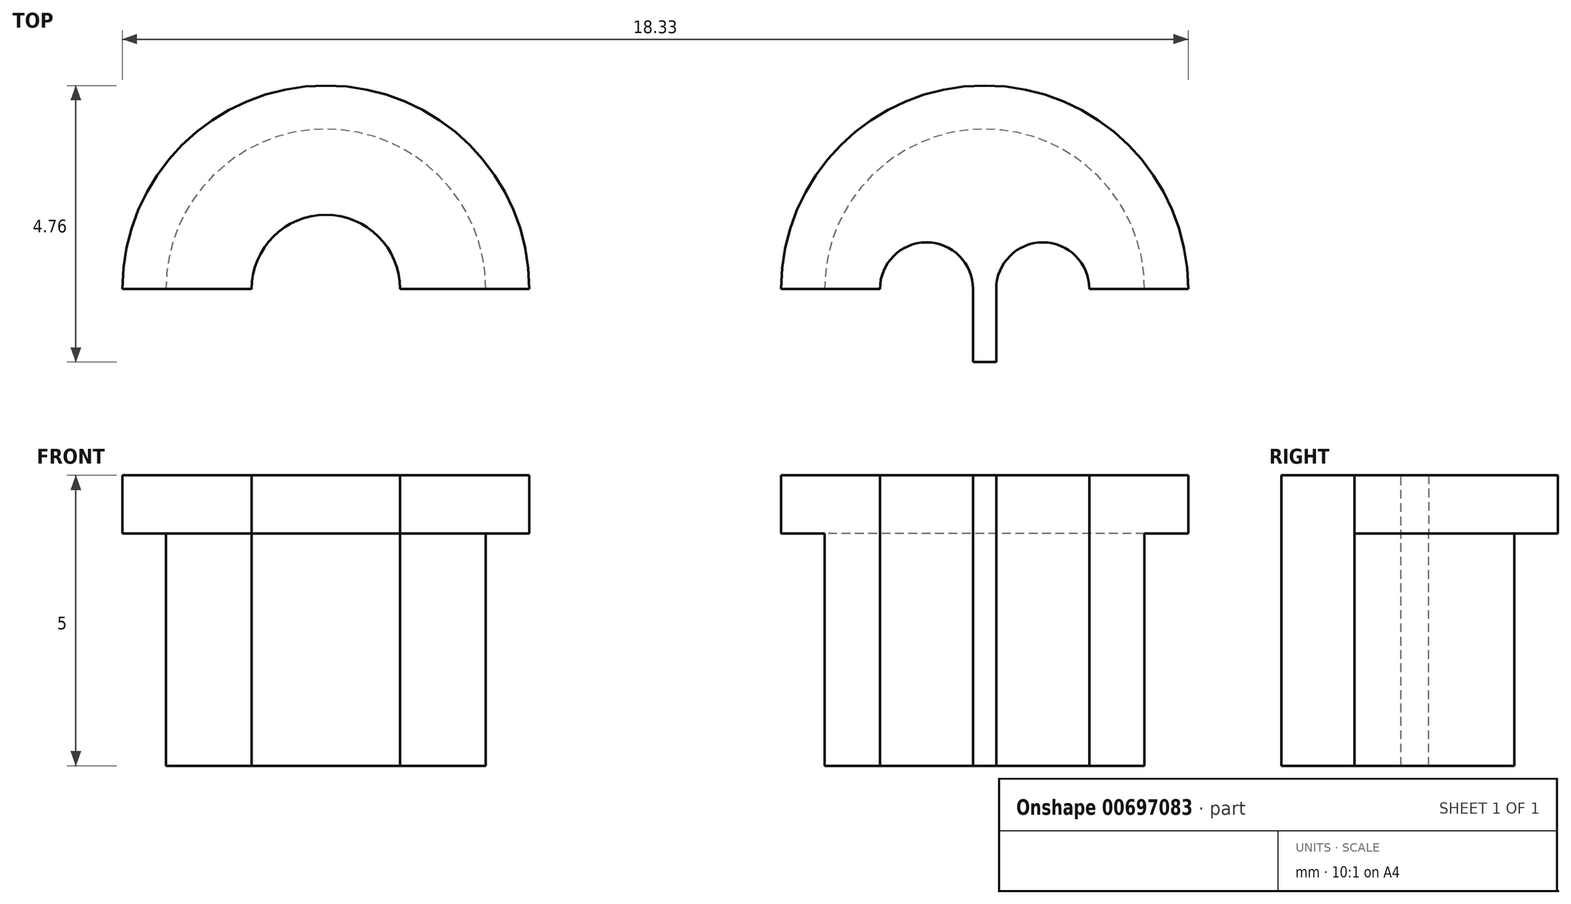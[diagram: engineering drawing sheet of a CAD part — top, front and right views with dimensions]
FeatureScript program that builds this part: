
annotation { "Feature Type Name" : "Feature", "Feature Type Description" : "" }
export const myFeature = defineFeature(function(context is Context, id is Id, definition is map)
    precondition{}
    {
        {
            assignVariable(context, id + "F0", {"name" : "thickness_washer", "anyValue" : 4 * mm});
        }
        {
            assignVariable(context, id + "F1", {"name" : "lip_thickness", "anyValue" : 1 * mm});
        }
        {
            var Q0;
            Q0=qCreatedBy(makeId("Top.planeOp"),FACE);
            var sketch = newSketch(context, id + "F2", { "sketchPlane" : qUnion([Q0])});
            skArc(sketch, "E0", {"start": v(2.75, 0) * mm, "mid": v(0, 2.75) * mm, "end": v(-2.75, 0) * mm});
            skPoint(sketch, "E1", {"position": v(-1, 0) * mm});
            skPoint(sketch, "E2", {"position": v(1, 0) * mm});
            skLineSegment(sketch, "E3", {"start": v(-2.75, 0) * mm, "end": v(-1.8, 0) * mm});
            skArc(sketch, "E4", {"start": v(-0.2, 0) * mm, "mid": v(-1, 0.8) * mm, "end": v(-1.8, 0) * mm});
            skArc(sketch, "E5", {"start": v(1.8, 0) * mm, "mid": v(1, 0.8) * mm, "end": v(0.2, 0) * mm});
            skLineSegment(sketch, "E6.trimOffspring", {"start": v(1.8, 0) * mm, "end": v(2.75, 0) * mm});
            skArc(sketch, "E7", {"start": v(3.5, 0) * mm, "mid": v(0, 3.5) * mm, "end": v(-3.5, 0) * mm});
            skLineSegment(sketch, "E8", {"start": v(3.5, 0) * mm, "end": v(0.2, 0) * mm});
            skLineSegment(sketch, "E9.trimOffspring", {"start": v(-0.2, 0) * mm, "end": v(-3.5, 0) * mm});
            skLineSegment(sketch, "E10", {"start": v(-0.2, 0) * mm, "end": v(-0.2, -1.26) * mm});
            skLineSegment(sketch, "E11", {"start": v(-0.2, -1.26) * mm, "end": v(0.2, -1.26) * mm});
            skLineSegment(sketch, "E12", {"start": v(0.2, -1.26) * mm, "end": v(0.2, 0) * mm});
            skArc(sketch, "E13", {"start": v(-8.58, 0) * mm, "mid": v(-11.33, 2.75) * mm, "end": v(-14.08, 0) * mm});
            skArc(sketch, "E14", {"start": v(-7.83, 0) * mm, "mid": v(-11.33, 3.5) * mm, "end": v(-14.83, 0) * mm});
            skLineSegment(sketch, "E15", {"start": v(-14.83, 0) * mm, "end": v(-14.08, 0) * mm});
            skLineSegment(sketch, "E16", {"start": v(-8.58, 0) * mm, "end": v(-7.83, 0) * mm});
            skArc(sketch, "E17", {"start": v(-10.05, 0) * mm, "mid": v(-11.33, 1.28) * mm, "end": v(-12.6, 0) * mm});
            skLineSegment(sketch, "E18", {"start": v(-14.08, 0) * mm, "end": v(-12.6, 0) * mm});
            skLineSegment(sketch, "E19", {"start": v(-10.05, 0) * mm, "end": v(-8.58, 0) * mm});
            skSolve(sketch);
        }
        {
            var Q0;
            Q0=makeQuery(id+"F2.imprint","IMPRINT",FACE,{"disambiguationData":[TD([[makeQuery(id+"F2.imprint","IMPRINT",EDGE,{"derivedFrom":sQuery(id+"F2.wireOp",EDGE,"E0")}),1.0]])]});
            extrude(context, id + "F3", {"entities" : qUnion([Q0]), "oppositeDirection" : true, "depth" : getVariable(context, 'thickness_washer'), "offsetDistance" : 25 * mm});
        }
        {
            var Q0;
            Q0=makeQuery(id+"F2.imprint","IMPRINT",FACE,{"disambiguationData":[TD([[makeQuery(id+"F2.imprint","IMPRINT",EDGE,{"derivedFrom":sQuery(id+"F2.wireOp",EDGE,"E0")}),-1.0]])]});
            var Q1;
            Q1=makeQuery(id+"F2.imprint","IMPRINT",FACE,{"disambiguationData":[TD([[makeQuery(id+"F2.imprint","IMPRINT",EDGE,{"derivedFrom":sQuery(id+"F2.wireOp",EDGE,"E0")}),1.0]])]});
            extrude(context, id + "F4", {"entities" : qUnion([Q0, Q1]), "operationType" : NewBodyOperationType.ADD, "depth" : getVariable(context, 'lip_thickness'), "offsetDistance" : 25 * mm});
        }
        {
            var Q0;
            Q0=makeQuery(id+"F2.imprint","IMPRINT",FACE,{"disambiguationData":[TD([[makeQuery(id+"F2.imprint","IMPRINT",EDGE,{"derivedFrom":sQuery(id+"F2.wireOp",EDGE,"E13")}),1.0]])]});
            extrude(context, id + "F5", {"entities" : qUnion([Q0]), "oppositeDirection" : true, "depth" : getVariable(context, 'thickness_washer'), "offsetDistance" : 25 * mm});
        }
        {
            var Q0;
            Q0=makeQuery(id+"F2.imprint","IMPRINT",FACE,{"disambiguationData":[TD([[makeQuery(id+"F2.imprint","IMPRINT",EDGE,{"derivedFrom":sQuery(id+"F2.wireOp",EDGE,"E13")}),1.0]])]});
            var Q1;
            Q1=makeQuery(id+"F2.imprint","IMPRINT",FACE,{"disambiguationData":[TD([[makeQuery(id+"F2.imprint","IMPRINT",EDGE,{"derivedFrom":sQuery(id+"F2.wireOp",EDGE,"E13")}),-1.0]])]});
            extrude(context, id + "F6", {"entities" : qUnion([Q0, Q1]), "depth" : getVariable(context, 'lip_thickness'), "offsetDistance" : 25 * mm});
        }
    });
